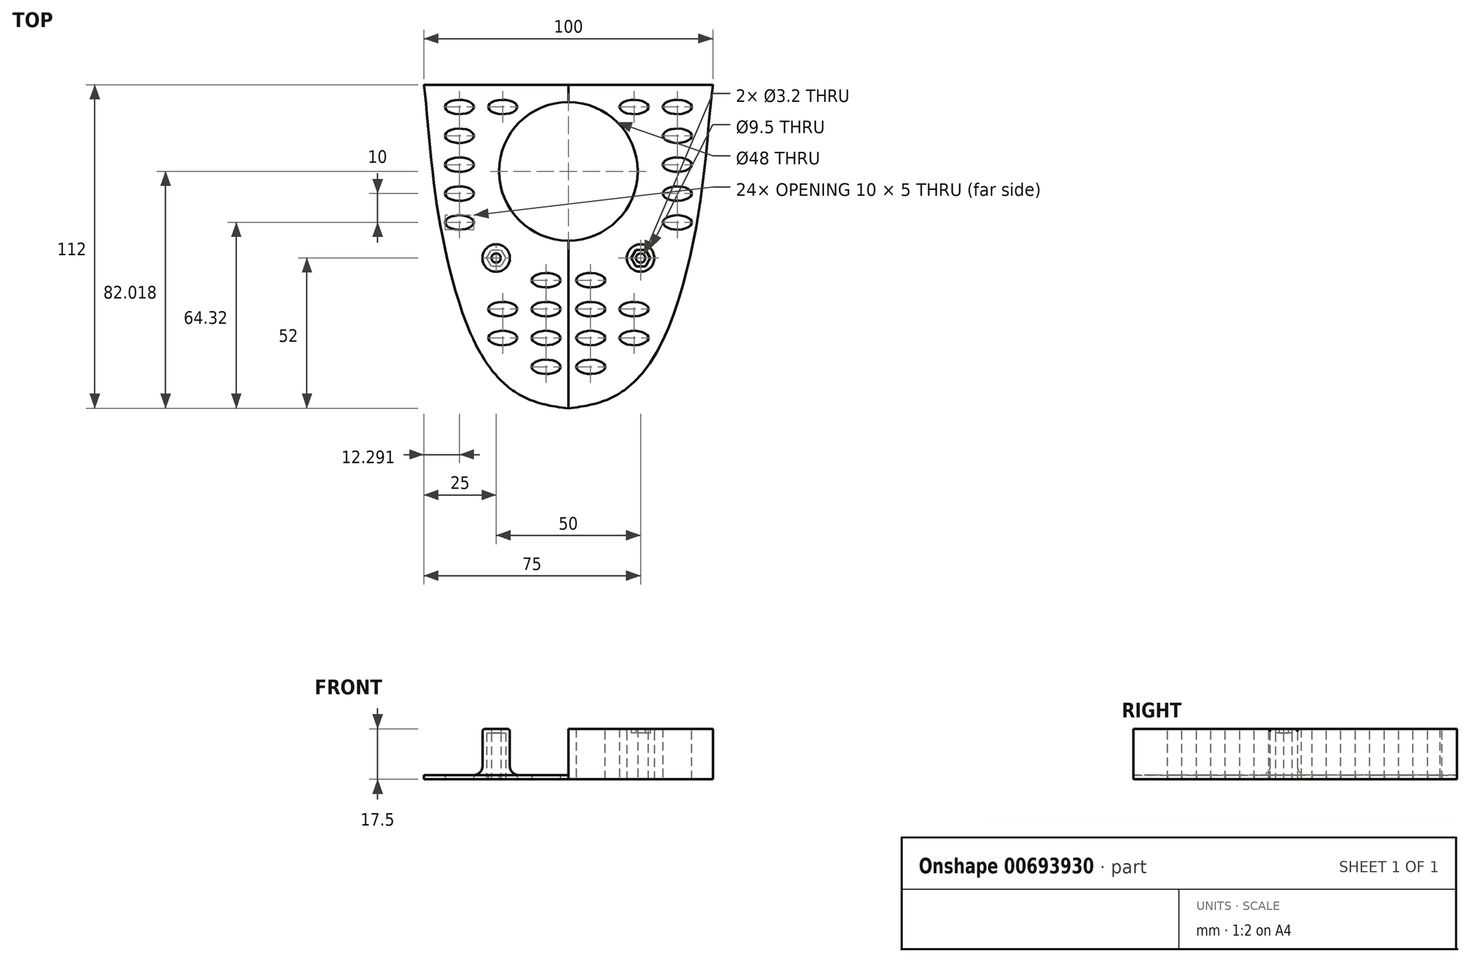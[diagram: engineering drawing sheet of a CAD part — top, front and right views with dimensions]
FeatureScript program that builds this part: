
annotation { "Feature Type Name" : "Feature", "Feature Type Description" : "" }
export const myFeature = defineFeature(function(context is Context, id is Id, definition is map)
    precondition{}
    {
        {
            var Q0;
            Q0=qCreatedBy(makeId("Top.planeOp"),FACE);
            var sketch = newSketch(context, id + "F0", { "sketchPlane" : qUnion([Q0])});
            skLineSegment(sketch, "E0", {"start": v(0, 74.75) * mm, "end": v(50, 74.75) * mm});
            skLineSegment(sketch, "E1", {"start": v(0, 74.75) * mm, "end": v(0, -37.25) * mm});
            skFitSpline(sketch, "E2", {"points": [v(50, 74.75) * mm, v(47, 44.75) * mm, v(42, 14.75) * mm, v(32, -15.25) * mm, v(19, -31.25) * mm, v(0, -37.25) * mm], "startDerivative": vector(-13.36, -107.56) * mm, "endDerivative": vector(-138.13, -13.22) * mm});
            skLineSegment(sketch, "E3.MirrorCS", {"start": v(0, 74.75) * mm, "end": v(-50, 74.75) * mm});
            skFitSpline(sketch, "E4.MirrorCS", {"points": [v(-50, 74.75) * mm, v(-47, 44.75) * mm, v(-42, 14.75) * mm, v(-32, -15.25) * mm, v(-19, -31.25) * mm, v(0, -37.25) * mm], "startDerivative": vector(13.36, -107.56) * mm, "endDerivative": vector(138.13, -13.22) * mm});
            skLineSegment(sketch, "E5.left", {"start": v(0, 69.67) * mm, "end": v(0, 64.67) * mm});
            skLineSegment(sketch, "E6.top", {"start": v(20, -58.33) * mm, "end": v(-20, -58.33) * mm});
            skLineSegment(sketch, "E6.left", {"start": v(20, 7.67) * mm, "end": v(20, -58.33) * mm});
            skLineSegment(sketch, "E6.right", {"start": v(-20, 7.67) * mm, "end": v(-20, -58.33) * mm});
            skPoint(sketch, "E6.middle", {"position": v(0, -25.33) * mm});
            skCircle(sketch, "E7", {"center": v(0, 44.77) * mm, "radius": 24 * mm});
            skCircle(sketch, "E8.cCircle", {"center": v(-25, 14.75) * mm, "radius": 2.85 * mm, "construction": true});
            skLineSegment(sketch, "E8.0", {"start": v(-26.65, 17.6) * mm, "end": v(-23.35, 17.6) * mm});
            skLineSegment(sketch, "E8.1", {"start": v(-23.35, 17.6) * mm, "end": v(-21.7, 14.75) * mm});
            skLineSegment(sketch, "E8.2", {"start": v(-21.7, 14.75) * mm, "end": v(-23.35, 11.9) * mm});
            skLineSegment(sketch, "E8.3", {"start": v(-23.35, 11.9) * mm, "end": v(-26.65, 11.9) * mm});
            skLineSegment(sketch, "E8.4", {"start": v(-26.65, 11.9) * mm, "end": v(-28.3, 14.75) * mm});
            skLineSegment(sketch, "E8.5", {"start": v(-28.3, 14.75) * mm, "end": v(-26.65, 17.6) * mm});
            skPoint(sketch, "E8.0.midPoint", {"position": v(-25, 17.6) * mm});
            skCircle(sketch, "E9", {"center": v(-25, 14.75) * mm, "radius": 4.75 * mm});
            skCircle(sketch, "E10", {"center": v(-25, 14.75) * mm, "radius": 1.6 * mm});
            skCircle(sketch, "E11.MirrorC", {"center": v(25, 14.75) * mm, "radius": 4.75 * mm});
            skLineSegment(sketch, "E12.MirrorCS", {"start": v(23.35, 17.6) * mm, "end": v(21.7, 14.75) * mm});
            skLineSegment(sketch, "E13.MirrorCS", {"start": v(21.7, 14.75) * mm, "end": v(23.35, 11.9) * mm});
            skLineSegment(sketch, "E14.MirrorCS", {"start": v(26.65, 17.6) * mm, "end": v(23.35, 17.6) * mm});
            skLineSegment(sketch, "E15.MirrorCS", {"start": v(28.3, 14.75) * mm, "end": v(26.65, 17.6) * mm});
            skLineSegment(sketch, "E16.MirrorCS", {"start": v(26.65, 11.9) * mm, "end": v(28.3, 14.75) * mm});
            skLineSegment(sketch, "E17.MirrorCS", {"start": v(23.35, 11.9) * mm, "end": v(26.65, 11.9) * mm});
            skCircle(sketch, "E18.MirrorC", {"center": v(25, 14.75) * mm, "radius": 1.6 * mm});
            skEllipse(sketch, "E19", {"center": v(-37.7, 67.07) * mm, "majorRadius": 5 * mm, "minorRadius": 2.5 * mm, "majorAxis": v(1, 0)});
            skEllipse(sketch, "E20.0.1.0", {"center": v(-37.7, 57.07) * mm, "majorRadius": 5 * mm, "minorRadius": 2.5 * mm, "majorAxis": v(1, 0)});
            skEllipse(sketch, "E20.0.2.0", {"center": v(-37.7, 47.07) * mm, "majorRadius": 5 * mm, "minorRadius": 2.5 * mm, "majorAxis": v(1, 0)});
            skEllipse(sketch, "E20.0.3.0", {"center": v(-37.7, 37.07) * mm, "majorRadius": 5 * mm, "minorRadius": 2.5 * mm, "majorAxis": v(1, 0)});
            skEllipse(sketch, "E20.0.4.0", {"center": v(-37.7, 27.07) * mm, "majorRadius": 5 * mm, "minorRadius": 2.5 * mm, "majorAxis": v(1, 0)});
            skEllipticalArc(sketch, "E20.0.8.0", {});
            skEllipse(sketch, "E20.1.0.0", {"center": v(-22.7, 67.07) * mm, "majorRadius": 5 * mm, "minorRadius": 2.5 * mm, "majorAxis": v(1, 0)});
            skEllipse(sketch, "E20.1.7.0", {"center": v(-22.7, -2.93) * mm, "majorRadius": 5 * mm, "minorRadius": 2.5 * mm, "majorAxis": v(1, 0)});
            skEllipse(sketch, "E20.1.8.0", {"center": v(-22.7, -12.93) * mm, "majorRadius": 5 * mm, "minorRadius": 2.5 * mm, "majorAxis": v(1, 0)});
            skEllipse(sketch, "E20.2.6.0", {"center": v(-7.7, 7.07) * mm, "majorRadius": 5 * mm, "minorRadius": 2.5 * mm, "majorAxis": v(1, 0)});
            skEllipse(sketch, "E20.2.7.0", {"center": v(-7.7, -2.93) * mm, "majorRadius": 5 * mm, "minorRadius": 2.5 * mm, "majorAxis": v(1, 0)});
            skEllipse(sketch, "E20.2.8.0", {"center": v(-7.7, -12.93) * mm, "majorRadius": 5 * mm, "minorRadius": 2.5 * mm, "majorAxis": v(1, 0)});
            skEllipse(sketch, "E20.2.9.0", {"center": v(-7.7, -22.93) * mm, "majorRadius": 5 * mm, "minorRadius": 2.5 * mm, "majorAxis": v(1, 0)});
            skLineSegment(sketch, "E20.direction1", {"start": v(-37.7, 67.07) * mm, "end": v(-22.7, 67.07) * mm, "construction": true});
            skLineSegment(sketch, "E20.direction2", {"start": v(-37.7, 67.07) * mm, "end": v(-37.7, 57.07) * mm, "construction": true});
            skEllipse(sketch, "E21.MirrorC", {"center": v(7.7, 7.07) * mm, "majorRadius": 5 * mm, "minorRadius": 2.5 * mm, "majorAxis": v(-1, 0)});
            skEllipse(sketch, "E22.MirrorC", {"center": v(7.7, -2.93) * mm, "majorRadius": 5 * mm, "minorRadius": 2.5 * mm, "majorAxis": v(-1, 0)});
            skEllipse(sketch, "E23.MirrorC", {"center": v(7.7, -12.93) * mm, "majorRadius": 5 * mm, "minorRadius": 2.5 * mm, "majorAxis": v(-1, 0)});
            skEllipse(sketch, "E24.MirrorC", {"center": v(7.7, -22.93) * mm, "majorRadius": 5 * mm, "minorRadius": 2.5 * mm, "majorAxis": v(-1, 0)});
            skEllipse(sketch, "E25.MirrorC", {"center": v(22.7, -12.93) * mm, "majorRadius": 5 * mm, "minorRadius": 2.5 * mm, "majorAxis": v(-1, 0)});
            skEllipse(sketch, "E26.MirrorC", {"center": v(22.7, -2.93) * mm, "majorRadius": 5 * mm, "minorRadius": 2.5 * mm, "majorAxis": v(-1, 0)});
            skEllipse(sketch, "E27.MirrorC", {"center": v(37.7, 27.07) * mm, "majorRadius": 5 * mm, "minorRadius": 2.5 * mm, "majorAxis": v(-1, 0)});
            skEllipse(sketch, "E28.MirrorC", {"center": v(37.7, 37.07) * mm, "majorRadius": 5 * mm, "minorRadius": 2.5 * mm, "majorAxis": v(-1, 0)});
            skEllipse(sketch, "E29.MirrorC", {"center": v(37.7, 47.07) * mm, "majorRadius": 5 * mm, "minorRadius": 2.5 * mm, "majorAxis": v(-1, 0)});
            skEllipse(sketch, "E30.MirrorC", {"center": v(37.7, 57.07) * mm, "majorRadius": 5 * mm, "minorRadius": 2.5 * mm, "majorAxis": v(-1, 0)});
            skEllipse(sketch, "E31.MirrorC", {"center": v(22.7, 67.07) * mm, "majorRadius": 5 * mm, "minorRadius": 2.5 * mm, "majorAxis": v(-1, 0)});
            skEllipse(sketch, "E32.MirrorC", {"center": v(37.7, 67.07) * mm, "majorRadius": 5 * mm, "minorRadius": 2.5 * mm, "majorAxis": v(-1, 0)});
            const initialGuessF0  = {"E20.0.8.0": [-0.03770889341831207, -0.012929908502941026, 1, 0, 0.005, 0.0025, 6.046335062874113, 0.6839810852619316]};
            skSetInitialGuess(sketch, initialGuessF0);
            skSolve(sketch);
        }
        {
            var Q0;
            {var subQ6=sQuery(id+"F0.wireOp",EDGE,"E0");Q0=makeQuery(id+"F0.imprint","IMPRINT",FACE,{"disambiguationData":[TD([[makeQuery(id+"F0.imprint","IMPRINT",EDGE,{"derivedFrom":subQ6}),-1.0]])]});}
            var Q1;
            {var subQ1=sQuery(id+"F0.wireOp",EDGE,"E3.MirrorCS");Q1=makeQuery(id+"F0.imprint","IMPRINT",FACE,{"disambiguationData":[TD([[makeQuery(id+"F0.imprint","IMPRINT",EDGE,{"derivedFrom":subQ1}),1.0]])]});}
            var Q2;
            {var subQ5=sQuery(id+"F0.wireOp",EDGE,"TYK1jfoF-MM1W-zxum-rjPu-zrtXxGjDDHzP.right");Q2=makeQuery(id+"F0.imprint","IMPRINT",FACE,{"disambiguationData":[TD([[makeQuery(id+"F0.imprint","IMPRINT",EDGE,{"derivedFrom":subQ5}),1.0]])]});}
            var Q3;
            {var subQ5=sQuery(id+"F0.wireOp",EDGE,"TYK1jfoF-MM1W-zxum-rjPu-zrtXxGjDDHzP.left");Q3=makeQuery(id+"F0.imprint","IMPRINT",FACE,{"disambiguationData":[TD([[makeQuery(id+"F0.imprint","IMPRINT",EDGE,{"derivedFrom":subQ5}),-1.0]])]});}
            var Q4;
            Q4=makeQuery(id+"F0.imprint","IMPRINT",FACE,{"disambiguationData":[TD([[makeQuery(id+"F0.imprint","IMPRINT",EDGE,{"derivedFrom":sQuery(id+"F0.wireOp",EDGE,"WDIr4lwU-NEgI-fRgc-Ip0B-rQfDtMe4qve4")}),-1.0]])]});
            var Q5;
            Q5=makeQuery(id+"F0.imprint","IMPRINT",FACE,{"disambiguationData":[TD([[makeQuery(id+"F0.imprint","IMPRINT",EDGE,{"derivedFrom":sQuery(id+"F0.wireOp",EDGE,"edd84c66-71c7-4481-84ac-934ccea6ba530.MirrorC")}),1.0]])]});
            var Q6;
            {var subQ0=sQuery(id+"F0.wireOp",EDGE,"vB9Euivt-dF2E-eSBk-yy4G-zRBSllFoftQc");var subQ1=sQuery(id+"F0.wireOp",EDGE,"TYK1jfoF-MM1W-zxum-rjPu-zrtXxGjDDHzP.right");var subQ2=makeQuery(id+"F0.imprint","INTERSECT",VERTEX,{"derivedFrom":[subQ1,subQ0]});Q6=makeQuery(id+"F0.imprint","IMPRINT",FACE,{"disambiguationData":[TD([[makeQuery(id+"F0.imprint","IMPRINT",EDGE,{"disambiguationData":[TD([[subQ2,1.0]])],"derivedFrom":subQ1}),-1.0]])]});}
            var Q7;
            Q7=makeQuery(id+"F0.imprint","IMPRINT",FACE,{"disambiguationData":[TD([[makeQuery(id+"F0.imprint","IMPRINT",EDGE,{"derivedFrom":sQuery(id+"F0.wireOp",EDGE,"m5nDsKvf-8LoU-mvbZ-D9gW-mzCtwEUpFt8m")}),-1.0]])]});
            var Q8;
            {var subQ0=sQuery(id+"F0.wireOp",EDGE,"vB9Euivt-dF2E-eSBk-yy4G-zRBSllFoftQc");var subQ1=sQuery(id+"F0.wireOp",EDGE,"TYK1jfoF-MM1W-zxum-rjPu-zrtXxGjDDHzP.left");var subQ2=makeQuery(id+"F0.imprint","INTERSECT",VERTEX,{"derivedFrom":[subQ1,subQ0]});Q8=makeQuery(id+"F0.imprint","IMPRINT",FACE,{"disambiguationData":[TD([[makeQuery(id+"F0.imprint","IMPRINT",EDGE,{"disambiguationData":[TD([[subQ2,1.0]])],"derivedFrom":subQ1}),1.0]])]});}
            var Q9;
            Q9=makeQuery(id+"F0.imprint","IMPRINT",FACE,{"disambiguationData":[TD([[makeQuery(id+"F0.imprint","IMPRINT",EDGE,{"derivedFrom":sQuery(id+"F0.wireOp",EDGE,"4bb37ab7-d421-4cb6-9f96-0a3fbe90f1960.MirrorC")}),1.0]])]});
            var Q10;
            {var subQ3=sQuery(id+"F0.wireOp",EDGE,"E6.bottom");var subQ5=sQuery(id+"F0.wireOp",EDGE,"E6.right");var subQ7=makeQuery(id+"F0.imprint","INTERSECT",VERTEX,{"derivedFrom":[subQ3,subQ5]});Q10=makeQuery(id+"F0.imprint","IMPRINT",FACE,{"disambiguationData":[TD([[makeQuery(id+"F0.imprint","IMPRINT",EDGE,{"disambiguationData":[TD([[subQ7,1.0]])],"derivedFrom":subQ3}),1.0]])]});}
            var Q11;
            {var subQ3=sQuery(id+"F0.wireOp",EDGE,"E6.bottom");var subQ5=sQuery(id+"F0.wireOp",EDGE,"E6.left");var subQ6=makeQuery(id+"F0.imprint","INTERSECT",VERTEX,{"derivedFrom":[subQ3,subQ5]});Q11=makeQuery(id+"F0.imprint","IMPRINT",FACE,{"disambiguationData":[TD([[makeQuery(id+"F0.imprint","IMPRINT",EDGE,{"disambiguationData":[TD([[subQ6,-1.0]])],"derivedFrom":subQ3}),1.0]])]});}
            var Q12;
            Q12=makeQuery(id+"F0.imprint","IMPRINT",FACE,{"disambiguationData":[TD([[makeQuery(id+"F0.imprint","IMPRINT",EDGE,{"derivedFrom":sQuery(id+"F0.wireOp",EDGE,"xv81IKlE-8eeK-npeu-qJmz-NVvhxvwPC5Cs")}),1.0]])]});
            var Q13;
            Q13=makeQuery(id+"F0.imprint","IMPRINT",FACE,{"disambiguationData":[TD([[makeQuery(id+"F0.imprint","IMPRINT",EDGE,{"derivedFrom":sQuery(id+"F0.wireOp",EDGE,"4WyMCeIH-wfKK-O0CN-jhJr-EVKcvJlUJ06v")}),1.0]])]});
            var Q14;
            Q14=makeQuery(id+"F0.imprint","IMPRINT",FACE,{"disambiguationData":[TD([[makeQuery(id+"F0.imprint","IMPRINT",EDGE,{"derivedFrom":sQuery(id+"F0.wireOp",EDGE,"7HEiTd4f-LGHk-PhaP-TUIV-b1b3WvIRwaOs")}),1.0]])]});
            var Q15;
            Q15=makeQuery(id+"F0.imprint","IMPRINT",FACE,{"disambiguationData":[TD([[makeQuery(id+"F0.imprint","IMPRINT",EDGE,{"derivedFrom":sQuery(id+"F0.wireOp",EDGE,"aNhq8VAy-Ns4E-n56P-tuef-qBzbECUYGK5I")}),1.0]])]});
            var Q16;
            Q16=makeQuery(id+"F0.imprint","IMPRINT",FACE,{"disambiguationData":[TD([[makeQuery(id+"F0.imprint","IMPRINT",EDGE,{"derivedFrom":sQuery(id+"F0.wireOp",EDGE,"9e1deac3-640c-4376-a571-affbd63c0bd70.MirrorC")}),-1.0]])]});
            var Q17;
            Q17=makeQuery(id+"F0.imprint","IMPRINT",FACE,{"disambiguationData":[TD([[makeQuery(id+"F0.imprint","IMPRINT",EDGE,{"derivedFrom":sQuery(id+"F0.wireOp",EDGE,"1ca89248-2e6e-442c-9f21-6806bc7b296d0.MirrorC")}),-1.0]])]});
            var Q18;
            Q18=makeQuery(id+"F0.imprint","IMPRINT",FACE,{"disambiguationData":[TD([[makeQuery(id+"F0.imprint","IMPRINT",EDGE,{"derivedFrom":sQuery(id+"F0.wireOp",EDGE,"c1e89451-e1c1-4668-9ca4-745382b146620.MirrorC")}),-1.0]])]});
            var Q19;
            {var subQ0=sQuery(id+"F0.wireOp",EDGE,"aff464dd-82a2-404e-9524-793c85fd9e030.MirrorC");var subQ1=sQuery(id+"F0.wireOp",EDGE,"E6.left");var subQ2=makeQuery(id+"F0.imprint","INTERSECT",VERTEX,{"disambiguationData":[OD(0.0)],"derivedFrom":[subQ1,subQ0]});Q19=makeQuery(id+"F0.imprint","IMPRINT",FACE,{"disambiguationData":[TD([[makeQuery(id+"F0.imprint","IMPRINT",EDGE,{"disambiguationData":[TD([[subQ2,-1.0]])],"derivedFrom":subQ1}),1.0]])]});}
            var Q20;
            {var subQ0=sQuery(id+"F0.wireOp",EDGE,"Xi9fobMV-gwtw-g7SW-i0rf-od4x8NfQZ1kA");var subQ1=sQuery(id+"F0.wireOp",EDGE,"E1");var subQ2=makeQuery(id+"F0.imprint","INTERSECT",VERTEX,{"disambiguationData":[OD(0.0)],"derivedFrom":[subQ1,subQ0]});Q20=makeQuery(id+"F0.imprint","IMPRINT",FACE,{"disambiguationData":[TD([[makeQuery(id+"F0.imprint","IMPRINT",EDGE,{"disambiguationData":[TD([[subQ2,-1.0]])],"derivedFrom":subQ1}),1.0]])]});}
            var Q21;
            {var subQ0=sQuery(id+"F0.wireOp",EDGE,"Xi9fobMV-gwtw-g7SW-i0rf-od4x8NfQZ1kA");var subQ1=sQuery(id+"F0.wireOp",EDGE,"E1");var subQ2=makeQuery(id+"F0.imprint","INTERSECT",VERTEX,{"disambiguationData":[OD(0.0)],"derivedFrom":[subQ1,subQ0]});Q21=makeQuery(id+"F0.imprint","IMPRINT",FACE,{"disambiguationData":[TD([[makeQuery(id+"F0.imprint","IMPRINT",EDGE,{"disambiguationData":[TD([[subQ2,-1.0]])],"derivedFrom":subQ1}),-1.0]])]});}
            var Q22;
            {var subQ0=sQuery(id+"F0.wireOp",EDGE,"yoYNCWBJ-a6Wv-L3ek-o0xD-EBqNdFQK8TOE");var subQ1=sQuery(id+"F0.wireOp",EDGE,"E6.right");var subQ2=makeQuery(id+"F0.imprint","INTERSECT",VERTEX,{"disambiguationData":[OD(0.0)],"derivedFrom":[subQ1,subQ0]});Q22=makeQuery(id+"F0.imprint","IMPRINT",FACE,{"disambiguationData":[TD([[makeQuery(id+"F0.imprint","IMPRINT",EDGE,{"disambiguationData":[TD([[subQ2,-1.0]])],"derivedFrom":subQ1}),-1.0]])]});}
            var Q23;
            {var subQ0=sQuery(id+"F0.wireOp",EDGE,"lKSrTgII-7dB3-NQrQ-qCJx-8DBmOwPrI0o2");var subQ1=sQuery(id+"F0.wireOp",EDGE,"E1");var subQ2=makeQuery(id+"F0.imprint","INTERSECT",VERTEX,{"disambiguationData":[OD(0.0)],"derivedFrom":[subQ1,subQ0]});Q23=makeQuery(id+"F0.imprint","IMPRINT",FACE,{"disambiguationData":[TD([[makeQuery(id+"F0.imprint","IMPRINT",EDGE,{"disambiguationData":[TD([[subQ2,-1.0]])],"derivedFrom":subQ1}),-1.0]])]});}
            var Q24;
            {var subQ0=sQuery(id+"F0.wireOp",EDGE,"lKSrTgII-7dB3-NQrQ-qCJx-8DBmOwPrI0o2");var subQ1=sQuery(id+"F0.wireOp",EDGE,"E1");var subQ2=makeQuery(id+"F0.imprint","INTERSECT",VERTEX,{"disambiguationData":[OD(0.0)],"derivedFrom":[subQ1,subQ0]});Q24=makeQuery(id+"F0.imprint","IMPRINT",FACE,{"disambiguationData":[TD([[makeQuery(id+"F0.imprint","IMPRINT",EDGE,{"disambiguationData":[TD([[subQ2,-1.0]])],"derivedFrom":subQ1}),1.0]])]});}
            var Q25;
            Q25=makeQuery(id+"F0.imprint","IMPRINT",FACE,{"disambiguationData":[TD([[makeQuery(id+"F0.imprint","IMPRINT",EDGE,{"derivedFrom":sQuery(id+"F0.wireOp",EDGE,"E8.0")}),1.0]])]});
            var Q26;
            Q26=makeQuery(id+"F0.imprint","IMPRINT",FACE,{"disambiguationData":[TD([[makeQuery(id+"F0.imprint","IMPRINT",EDGE,{"derivedFrom":sQuery(id+"F0.wireOp",EDGE,"E11.MirrorC")}),-1.0]])]});
            var Q27;
            {var subQ0=sQuery(id+"F0.wireOp",EDGE,"02qkhHRP-5zDQ-RhmV-amqG-HKLUPI6GVCv5.right");Q27=makeQuery(id+"F0.imprint","IMPRINT",FACE,{"disambiguationData":[TD([[makeQuery(id+"F0.imprint","IMPRINT",EDGE,{"derivedFrom":subQ0}),-1.0]])]});}
            var Q28;
            {var subQ0=sQuery(id+"F0.wireOp",EDGE,"02qkhHRP-5zDQ-RhmV-amqG-HKLUPI6GVCv5.left");Q28=makeQuery(id+"F0.imprint","IMPRINT",FACE,{"disambiguationData":[TD([[makeQuery(id+"F0.imprint","IMPRINT",EDGE,{"derivedFrom":subQ0}),1.0]])]});}
            var Q29;
            {var subQ0=sQuery(id+"F0.wireOp",EDGE,"E20.0.8.0");Q29=makeQuery(id+"F0.imprint","IMPRINT",FACE,{"disambiguationData":[TD([[makeQuery(id+"F0.imprint","IMPRINT",EDGE,{"derivedFrom":subQ0}),1.0]])]});}
            extrude(context, id + "F1", {"entities" : qUnion([Q0, Q1, Q2, Q3, Q4, Q5, Q6, Q7, Q8, Q9, Q10, Q11, Q12, Q13, Q14, Q15, Q16, Q17, Q18, Q19, Q20, Q21, Q22, Q23, Q24, Q25, Q26, Q27, Q28, Q29]), "depth" : 1.5 * mm, "offsetDistance" : 25 * mm});
        }
        {
            var Q0;
            Q0=makeQuery(id+"F0.imprint","IMPRINT",FACE,{"disambiguationData":[TD([[makeQuery(id+"F0.imprint","IMPRINT",EDGE,{"derivedFrom":sQuery(id+"F0.wireOp",EDGE,"E8.0")}),1.0]])]});
            var Q1;
            Q1=makeQuery(id+"F0.imprint","IMPRINT",FACE,{"disambiguationData":[TD([[makeQuery(id+"F0.imprint","IMPRINT",EDGE,{"derivedFrom":sQuery(id+"F0.wireOp",EDGE,"E11.MirrorC")}),-1.0]])]});
            extrude(context, id + "F2", {"entities" : qUnion([Q0, Q1]), "operationType" : NewBodyOperationType.ADD, "depth" : 16 * mm, "offsetDistance" : 25 * mm});
        }
        {
            var Q0;
            Q0=makeQuery(id+"F0.imprint","IMPRINT",FACE,{"disambiguationData":[TD([[makeQuery(id+"F0.imprint","IMPRINT",EDGE,{"derivedFrom":sQuery(id+"F0.wireOp",EDGE,"E8.0")}),-1.0]])]});
            var Q1;
            Q1=makeQuery(id+"F0.imprint","IMPRINT",FACE,{"disambiguationData":[TD([[makeQuery(id+"F0.imprint","IMPRINT",EDGE,{"derivedFrom":sQuery(id+"F0.wireOp",EDGE,"E8.0")}),1.0]])]});
            var Q2;
            Q2=makeQuery(id+"F0.imprint","IMPRINT",FACE,{"disambiguationData":[TD([[makeQuery(id+"F0.imprint","IMPRINT",EDGE,{"derivedFrom":sQuery(id+"F0.wireOp",EDGE,"E11.MirrorC")}),-1.0]])]});
            var Q3;
            Q3=makeQuery(id+"F0.imprint","IMPRINT",FACE,{"disambiguationData":[TD([[makeQuery(id+"F0.imprint","IMPRINT",EDGE,{"derivedFrom":sQuery(id+"F0.wireOp",EDGE,"E12.MirrorCS")}),1.0]])]});
            extrude(context, id + "F3", {"entities" : qUnion([Q0, Q1, Q2, Q3]), "operationType" : NewBodyOperationType.ADD, "depth" : 17.5 * mm, "offsetDistance" : 25 * mm, "hasSecondDirection" : true, "secondDirectionOppositeDirection" : false, "secondDirectionDepth" : 16 * mm});
        }
        {
            var Q0;
            Q0=makeQuery(id+"F2.boolean.opBoolean","INTERSECT",EDGE,{"derivedFrom":[makeQuery(id+"F1.opExtrude","CAP_FACE",FACE,{"disambiguationData":[OSD([sQuery(id+"F0.wireOp",EDGE,"E0"),sQuery(id+"F0.wireOp",EDGE,"E2"),sQuery(id+"F0.wireOp",EDGE,"E3.MirrorCS"),sQuery(id+"F0.wireOp",EDGE,"E4.MirrorCS"),sQuery(id+"F0.wireOp",EDGE,"E7"),sQuery(id+"F0.wireOp",EDGE,"E8.0"),sQuery(id+"F0.wireOp",EDGE,"E8.1"),sQuery(id+"F0.wireOp",EDGE,"E8.2"),sQuery(id+"F0.wireOp",EDGE,"E8.3"),sQuery(id+"F0.wireOp",EDGE,"E8.4"),sQuery(id+"F0.wireOp",EDGE,"E8.5")])],"isStart":false}),makeQuery(id+"F2.opExtrude","SWEPT_FACE",FACE,{"disambiguationData":[OSD([sQuery(id+"F0.wireOp",EDGE,"E9")])]})]});
            var Q1;
            Q1=makeQuery(id+"F2.boolean.opBoolean","INTERSECT",EDGE,{"derivedFrom":[makeQuery(id+"F1.opExtrude","CAP_FACE",FACE,{"disambiguationData":[OSD([sQuery(id+"F0.wireOp",EDGE,"E0"),sQuery(id+"F0.wireOp",EDGE,"E2"),sQuery(id+"F0.wireOp",EDGE,"E3.MirrorCS"),sQuery(id+"F0.wireOp",EDGE,"E4.MirrorCS"),sQuery(id+"F0.wireOp",EDGE,"E6.left"),sQuery(id+"F0.wireOp",EDGE,"E6.right"),sQuery(id+"F0.wireOp",EDGE,"E7"),sQuery(id+"F0.wireOp",EDGE,"E8.0"),sQuery(id+"F0.wireOp",EDGE,"E8.1"),sQuery(id+"F0.wireOp",EDGE,"E8.2"),sQuery(id+"F0.wireOp",EDGE,"E8.3"),sQuery(id+"F0.wireOp",EDGE,"E8.4"),sQuery(id+"F0.wireOp",EDGE,"E8.5"),sQuery(id+"F0.wireOp",EDGE,"E12.MirrorCS"),sQuery(id+"F0.wireOp",EDGE,"E13.MirrorCS"),sQuery(id+"F0.wireOp",EDGE,"E14.MirrorCS"),sQuery(id+"F0.wireOp",EDGE,"E15.MirrorCS"),sQuery(id+"F0.wireOp",EDGE,"E16.MirrorCS"),sQuery(id+"F0.wireOp",EDGE,"E17.MirrorCS")])],"isStart":false}),makeQuery(id+"F2.opExtrude","SWEPT_FACE",FACE,{"disambiguationData":[OSD([sQuery(id+"F0.wireOp",EDGE,"E11.MirrorC")])]})]});
            fillet(context, id + "F4", {"entities" : qUnion([Q0, Q1]), "radius" : 3 * mm, "tangentPropagation" : true, "allowEdgeOverflow" : false});
        }
        {
            var Q0;
            Q0=makeQuery(id+"F3.opExtrude","CAP_EDGE",EDGE,{"disambiguationData":[OSD([sQuery(id+"F0.wireOp",EDGE,"E9")])],"isStart":false});
            var Q1;
            Q1=makeQuery(id+"F3.opExtrude","CAP_EDGE",EDGE,{"disambiguationData":[OSD([sQuery(id+"F0.wireOp",EDGE,"E11.MirrorC")])],"isStart":false});
            fillet(context, id + "F5", {"entities" : qUnion([Q0, Q1]), "radius" : 1 * mm, "tangentPropagation" : true, "allowEdgeOverflow" : false});
        }
    });
